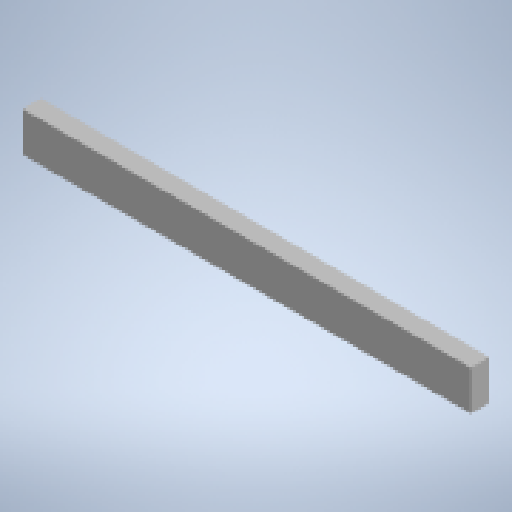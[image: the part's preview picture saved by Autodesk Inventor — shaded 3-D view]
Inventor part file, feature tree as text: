
AUTODESK INVENTOR PART (.ipt)
format: ipt  version: 2023 (Build 270158000, 158)  size: 128,512 bytes
history: native  units: in
note: dims shown in document units (in); Inventor stores cm internally (conversion verified against a paired STEP export)
features: extrude x1, sketch x1
ambient origin geometry x8: Origin, YZ Plane, XZ Plane, XY Plane, X Axis, Y Axis, Z Axis, Center Point
bodies: Solid1 (feature_tree)
feature tree (2):
  extrude  "Extrusion1"  Depth=3.75in
  sketch  "Sketch1"  dims[d0=1.75in d1=3.75in d2=42.5in d3=0.0in]
